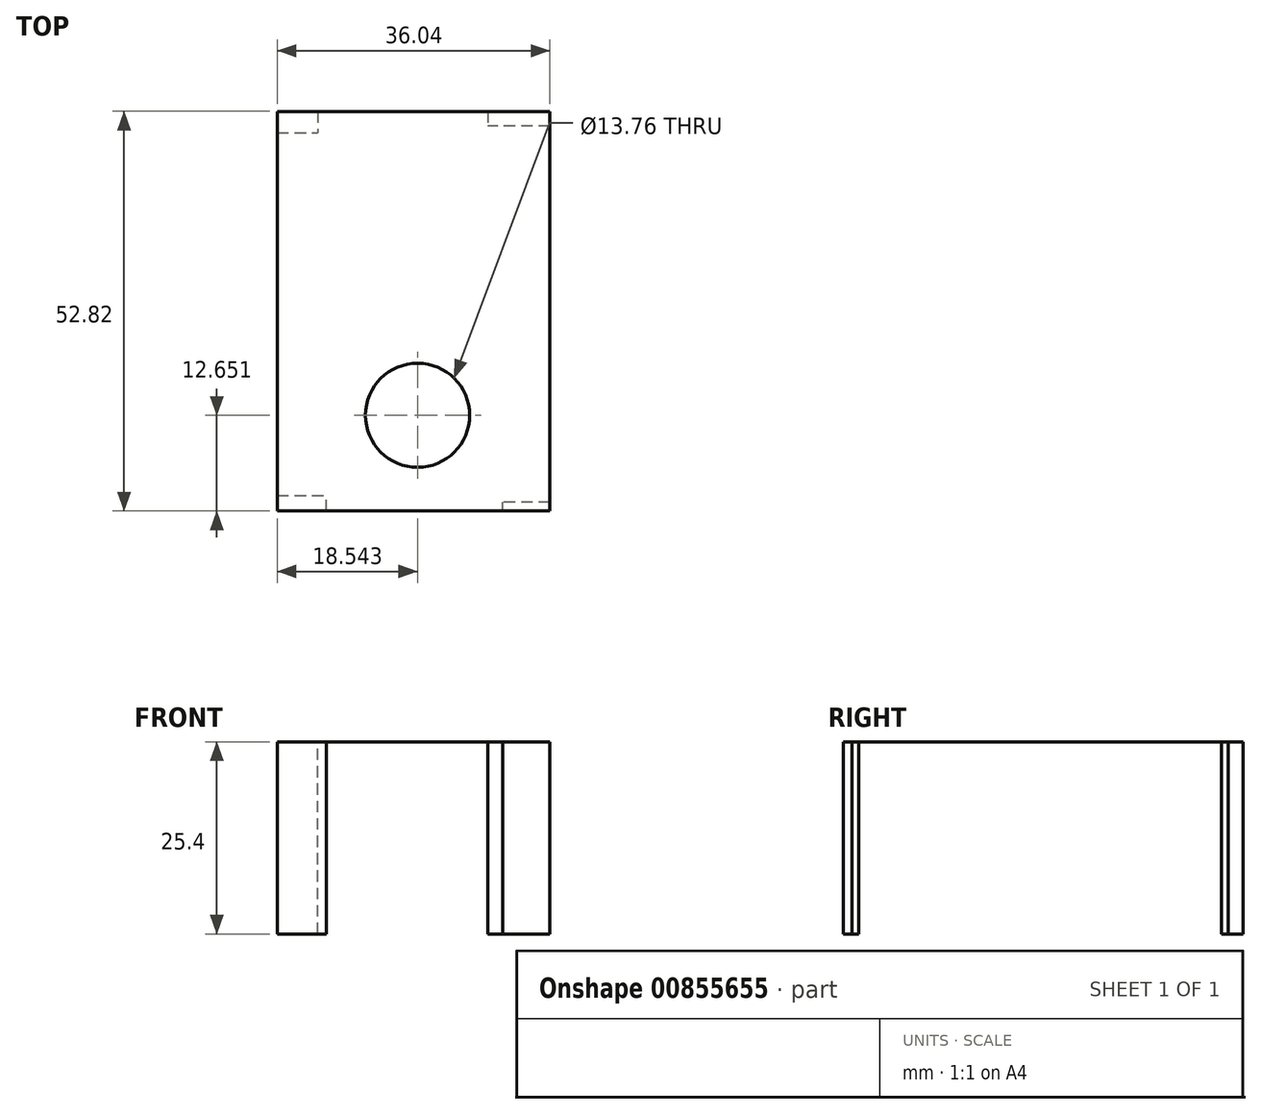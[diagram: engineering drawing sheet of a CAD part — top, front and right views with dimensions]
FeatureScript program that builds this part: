
annotation { "Feature Type Name" : "Feature", "Feature Type Description" : "" }
export const myFeature = defineFeature(function(context is Context, id is Id, definition is map)
    precondition{}
    {
        {
            var Q0;
            Q0=qCreatedBy(makeId("Top.planeOp"),FACE);
            var sketch = newSketch(context, id + "F0", { "sketchPlane" : qUnion([Q0])});
            skLineSegment(sketch, "E0.bottom", {"start": v(0, 0) * mm, "end": v(36.04, 0) * mm});
            skLineSegment(sketch, "E0.top", {"start": v(0, 52.82) * mm, "end": v(36.04, 52.82) * mm});
            skLineSegment(sketch, "E0.left", {"start": v(0, 0) * mm, "end": v(0, 52.82) * mm});
            skLineSegment(sketch, "E0.right", {"start": v(36.04, 0) * mm, "end": v(36.04, 52.82) * mm});
            skCircle(sketch, "E1", {"center": v(18.54, 12.65) * mm, "radius": 6.88 * mm});
            skSolve(sketch);
        }
        {
            var Q0;
            Q0=makeQuery(id+"F0.imprint","IMPRINT",FACE,{"disambiguationData":[TD([[makeQuery(id+"F0.imprint","IMPRINT",EDGE,{"derivedFrom":sQuery(id+"F0.wireOp",EDGE,"E0.bottom")}),1.0]])]});
            extrude(context, id + "F1", {"entities" : qUnion([Q0]), "depth" : 0.03 * mm, "offsetDistance" : 25.4 * mm});
        }
        {
            var Q0;
            Q0=makeQuery(id+"F1.opExtrude","CAP_FACE",FACE,{"disambiguationData":[OSD([sQuery(id+"F0.wireOp",EDGE,"E0.bottom"),sQuery(id+"F0.wireOp",EDGE,"E0.top"),sQuery(id+"F0.wireOp",EDGE,"E0.left"),sQuery(id+"F0.wireOp",EDGE,"E0.right"),sQuery(id+"F0.wireOp",EDGE,"E1")])],"isStart":false});
            var sketch = newSketch(context, id + "F2", { "sketchPlane" : qUnion([Q0])});
            skLineSegment(sketch, "E2.bottom", {"start": v(36.04, 0) * mm, "end": v(29.8, 0) * mm});
            skLineSegment(sketch, "E2.top", {"start": v(36.04, 1.13) * mm, "end": v(29.8, 1.13) * mm});
            skLineSegment(sketch, "E2.left", {"start": v(36.04, 0) * mm, "end": v(36.04, 1.13) * mm});
            skLineSegment(sketch, "E2.right", {"start": v(29.8, 0) * mm, "end": v(29.8, 1.13) * mm});
            skLineSegment(sketch, "E3.bottom", {"start": v(0, 0) * mm, "end": v(6.47, 0) * mm});
            skLineSegment(sketch, "E3.top", {"start": v(0, 2.03) * mm, "end": v(6.47, 2.03) * mm});
            skLineSegment(sketch, "E3.left", {"start": v(0, 0) * mm, "end": v(0, 2.03) * mm});
            skLineSegment(sketch, "E3.right", {"start": v(6.47, 0) * mm, "end": v(6.47, 2.03) * mm});
            skLineSegment(sketch, "E4.bottom", {"start": v(36.04, 52.82) * mm, "end": v(27.8, 52.82) * mm});
            skLineSegment(sketch, "E4.top", {"start": v(36.04, 50.87) * mm, "end": v(27.8, 50.87) * mm});
            skLineSegment(sketch, "E4.left", {"start": v(36.04, 52.82) * mm, "end": v(36.04, 50.87) * mm});
            skLineSegment(sketch, "E4.right", {"start": v(27.8, 52.82) * mm, "end": v(27.8, 50.87) * mm});
            skLineSegment(sketch, "E5.bottom", {"start": v(0, 52.82) * mm, "end": v(5.34, 52.82) * mm});
            skLineSegment(sketch, "E5.top", {"start": v(0, 49.97) * mm, "end": v(5.34, 49.97) * mm});
            skLineSegment(sketch, "E5.left", {"start": v(0, 52.82) * mm, "end": v(0, 49.97) * mm});
            skLineSegment(sketch, "E5.right", {"start": v(5.34, 52.82) * mm, "end": v(5.34, 49.97) * mm});
            skSolve(sketch);
        }
        {
            var Q0;
            Q0 = qSketchRegion(id + "F2", true);
            extrude(context, id + "F3", {"entities" : qUnion([Q0]), "operationType" : NewBodyOperationType.ADD, "oppositeDirection" : true, "depth" : 25.4 * mm, "offsetDistance" : 25.4 * mm});
        }
    });
